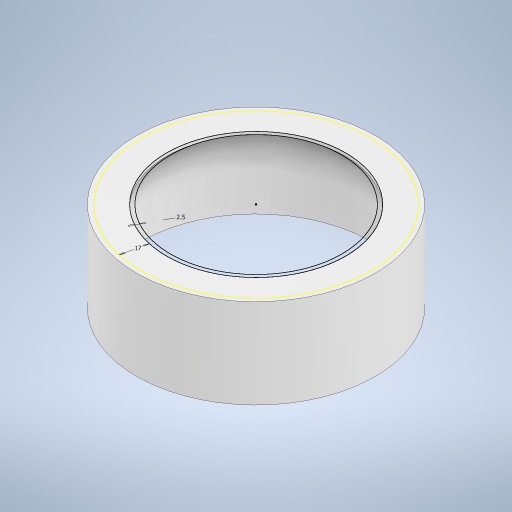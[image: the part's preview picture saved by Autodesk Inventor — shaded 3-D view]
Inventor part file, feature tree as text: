
AUTODESK INVENTOR PART (.ipt)
format: ipt  version: 2023 (Build 270158000, 158)  size: 592,384 bytes
history: native  units: mm
features: extrude x2, sketch x2
ambient origin geometry x8: Origin, YZ Plane, XZ Plane, XY Plane, X Axis, Y Axis, Z Axis, Center Point
bodies: Solid1 (feature_tree)
feature tree (4):
  extrude  "Extrusion1"  Depth=3.0mm
  sketch  "Sketch2"  dims[d2=60.0mm d3=0.0mm d4=17.0mm d5=2.5mm d6=2.0mm d7=0.0mm]
  extrude  "Extrusion2"  Depth=2.0mm
  sketch  "Sketch1"  dims[d0=160.0mm d1=3.0mm]
